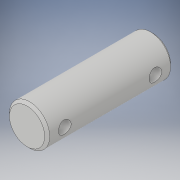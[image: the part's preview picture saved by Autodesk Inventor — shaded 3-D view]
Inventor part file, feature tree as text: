
AUTODESK INVENTOR PART (.ipt)
format: ipt  version: 2017 (Build 210142000, 142)  size: 119,808 bytes
history: native  units: mm
features: extrude x2, chamfer x2, sketch x2, plane x1
ambient origin geometry x8: Origin, YZ Plane, XZ Plane, XY Plane, X Axis, Y Axis, Z Axis, Center Point
bodies: Solid1 (feature_tree)
feature tree (7):
  extrude  "Extrusion1"  Depth=25.0mm TaperAngle=0.0deg
  chamfer  "Chamfer1"  Distance=0.5mm Angle=45.0deg
  chamfer  "Chamfer2"  Distance=0.5mm Angle=45.0deg
  plane  "Work Plane1"
  extrude  "Extrusion2"  Depth=2.5mm
  sketch  "Sketch2"  dims[d6=8.0mm d7=25.0mm d8=0.0mm d9=0.5mm d10=2.0mm d11=45.0deg d12=0.5mm d13=2.0mm d14=45.0deg]
  sketch  "Sketch3"  dims[d15=2.5mm d16=2.5mm d17=18.0mm d19=3.5mm d20=25.0mm d21=0.0mm]
